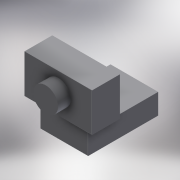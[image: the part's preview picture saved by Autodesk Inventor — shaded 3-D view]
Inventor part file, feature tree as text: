
AUTODESK INVENTOR PART (.ipt)
format: ipt  version: 2017 (Build 210142000, 142)  size: 186,368 bytes
history: native  units: mm
features: extrude x5, sketch x5, fillet x3, other x3, reference x2, projected_geometry x2
ambient origin geometry x8: Origin, YZ Plane, XZ Plane, XY Plane, X Axis, Y Axis, Z Axis, Center Point
bodies: Solid1 (feature_tree)
feature tree (20):
  extrude  "Extrusion1"  Depth=8.0mm
  extrude  "Extrusion2"  Depth=30.0mm
  extrude  "Extrusion3"  Depth=4.7mm TaperAngle=0.0deg
  extrude  "Extrusion4"  Depth=23.0mm
  fillet  "Fillet1"  Radius=5.0mm
  extrude  "Extrusion5"  Depth=20.5mm
  fillet  "Fillet2"  Radius=10.5mm
  fillet  "Fillet3"  Radius=3.0mm
  sketch  "Sketch1"  dims[d0=7.0mm d1=8.0mm]
  reference  "Reference1"
  reference  "Reference2"
  sketch  "Sketch2"  dims[d2=17.0mm d3=0.0mm d4=30.0mm]
  sketch  "Sketch3"  dims[d5=5.0mm d6=4.7mm d7=0.0mm]
  projected_geometry  "Projected Loop1"
  sketch  "Sketch4"  dims[d8=56.0mm d9=23.0mm d10=5.0mm]
  sketch  "Sketch5"  dims[d11=32.0mm d12=0.0mm d13=20.5mm d14=10.5mm d15=0.0mm d16=3.0mm d17=1.0mm d18=0.0mm d19=1.0mm d20=4.0mm]
  projected_geometry  "Projected Loop2"
  other  "<userpath>\Dropbox\Work\Project\Inventor\Base Assembly.iam"
  other  "Base Assembly.iam"
  other  "Camera mount:1"
